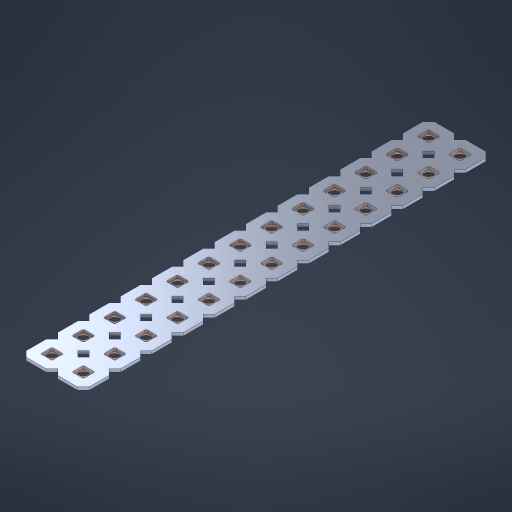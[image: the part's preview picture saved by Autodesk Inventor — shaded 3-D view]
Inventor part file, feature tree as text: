
AUTODESK INVENTOR PART (.ipt)
format: ipt  version: 2023 (Build 270158000, 158)  size: 549,376 bytes
history: native  units: in
note: dims shown in document units (in); Inventor stores cm internally (conversion verified against a paired STEP export)
features: other x27, extrude x25, sketch x2, pattern_linear x1
ambient origin geometry x8: Origin, YZ Plane, XZ Plane, XY Plane, X Axis, Y Axis, Z Axis, Center Point
bodies: Solid1 (feature_tree), Body (feature_tree)
feature tree (55):
  pattern_linear  "Rectangular Pattern1"  Spacing1=0.09in  [1 undecoded]
  sketch  "Sketch1"  dims[d1=0.5in]
  sketch  "Sketch2"  dims[d2=0.182in d3=0.09in d4=0.09in d5=0.09in d6=0.09in d7=0.09in d8=0.09in d9=0.09in d10=0.09in d11=0.02in d13=0.0in d14=0.172in d15=0.0625in d16=0.0in d19=0.5in d22=0.5in]
  other  "Srf1"
  other  "Srf126"
  other  "Srf127"
  other  "Srf128"
  other  "Srf129"
  other  "Srf130"
  other  "Srf131"
  other  "Srf250"
  other  "Srf251"
  other  "Srf252"
  other  "Srf253"
  other  "Srf254"
  other  "Srf255"
  other  "Srf268"
  other  "Srf269"
  other  "Srf270"
  other  "Srf271"
  other  "Srf272"
  other  "Srf273"
  other  "Srf274"
  other  "Srf275"
  other  "Srf276"
  other  "Srf277"
  other  "Srf278"
  other  "Srf279"
  other  "Srf280"
  other  "Circle"
  extrude  "ExtrusionSrf126"  Depth=0.09in
  extrude  "ExtrusionSrf127"  Depth=0.09in
  extrude  "ExtrusionSrf128"  Depth=0.09in
  extrude  "ExtrusionSrf129"  Depth=0.09in
  extrude  "ExtrusionSrf130"  Depth=0.09in
  extrude  "ExtrusionSrf131"  Depth=0.09in
  extrude  "ExtrusionSrf250"  Depth=0.09in
  extrude  "ExtrusionSrf251"  Depth=0.02in
  extrude  "ExtrusionSrf252"  TaperAngle=0.0deg  [1 undecoded]
  extrude  "ExtrusionSrf253"  Depth=0.5in
  extrude  "ExtrusionSrf254"  Depth=0.5in TaperAngle=0.0deg
  extrude  "ExtrusionSrf255"  Depth=0.5in
  extrude  "ExtrusionSrf268"  Depth=0.5in
  extrude  "ExtrusionSrf269"  [1 undecoded]
  extrude  "ExtrusionSrf270"  [1 undecoded]
  extrude  "ExtrusionSrf271"  [1 undecoded]
  extrude  "ExtrusionSrf272"  [1 undecoded]
  extrude  "ExtrusionSrf273"  [1 undecoded]
  extrude  "ExtrusionSrf274"  [1 undecoded]
  extrude  "ExtrusionSrf275"  [1 undecoded]
  extrude  "ExtrusionSrf276"  [1 undecoded]
  extrude  "ExtrusionSrf277"  [1 undecoded]
  extrude  "ExtrusionSrf278"  [1 undecoded]
  extrude  "ExtrusionSrf279"  [1 undecoded]
  extrude  "ExtrusionSrf280"  [1 undecoded]
note: 14 required parameter values undecoded (feature->parameter linkage not recoverable at this tier; creation-order binding heuristic only, values carry confidence <= 0.55)
